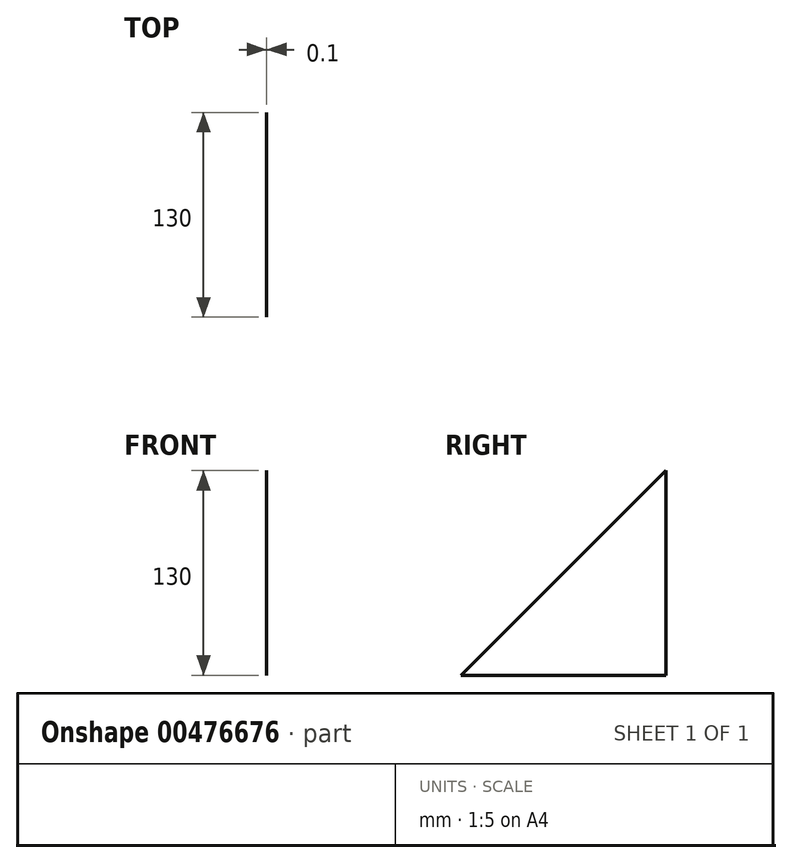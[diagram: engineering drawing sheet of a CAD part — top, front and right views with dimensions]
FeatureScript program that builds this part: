
annotation { "Feature Type Name" : "Feature", "Feature Type Description" : "" }
export const myFeature = defineFeature(function(context is Context, id is Id, definition is map)
    precondition{}
    {
        {
            var Q0;
            Q0=qCreatedBy(makeId("Right.planeOp"),FACE);
            var sketch = newSketch(context, id + "F0", { "sketchPlane" : qUnion([Q0])});
            skLineSegment(sketch, "E0", {"start": v(0, 0) * mm, "end": v(-130, 0) * mm});
            skLineSegment(sketch, "E1", {"start": v(-130, 0) * mm, "end": v(0, 130) * mm});
            skLineSegment(sketch, "E2", {"start": v(0, 130) * mm, "end": v(0, 0) * mm});
            skSolve(sketch);
        }
        {
            var Q0;
            Q0 = qSketchRegion(id + "F0", true);
            extrude(context, id + "F1", {"entities" : qUnion([Q0]), "depth" : 0.1 * mm});
        }
    });
